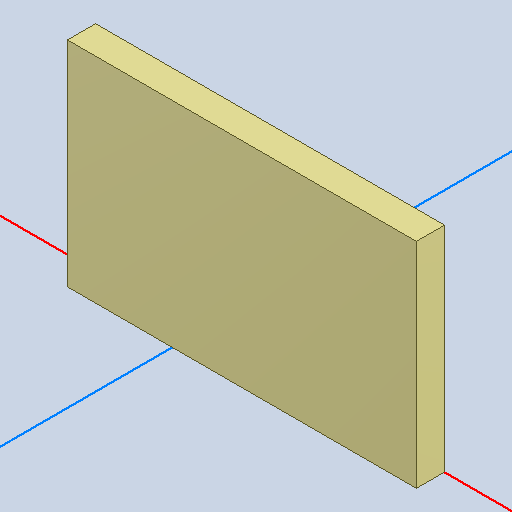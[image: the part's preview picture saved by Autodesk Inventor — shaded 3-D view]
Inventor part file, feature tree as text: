
AUTODESK INVENTOR PART (.ipt)
format: ipt  version: 2022 (Build 260153000, 153)  size: 90,112 bytes
history: native  units: mm
features: other x2, extrude x1
ambient origin geometry x8: Origin, YZ Plane, XZ Plane, XY Plane, X Axis, Y Axis, Z Axis, Center Point
bodies: Body1 (feature_tree)
feature tree (3):
  other  "Твердое тело1"
  extrude  "Выдавливание1"  Depth=1.0mm TaperAngle=0.0deg
  other  "SCREWTERMINAL-5MM-2, J1_SCREWTERMINAL-5MM-2_15"
